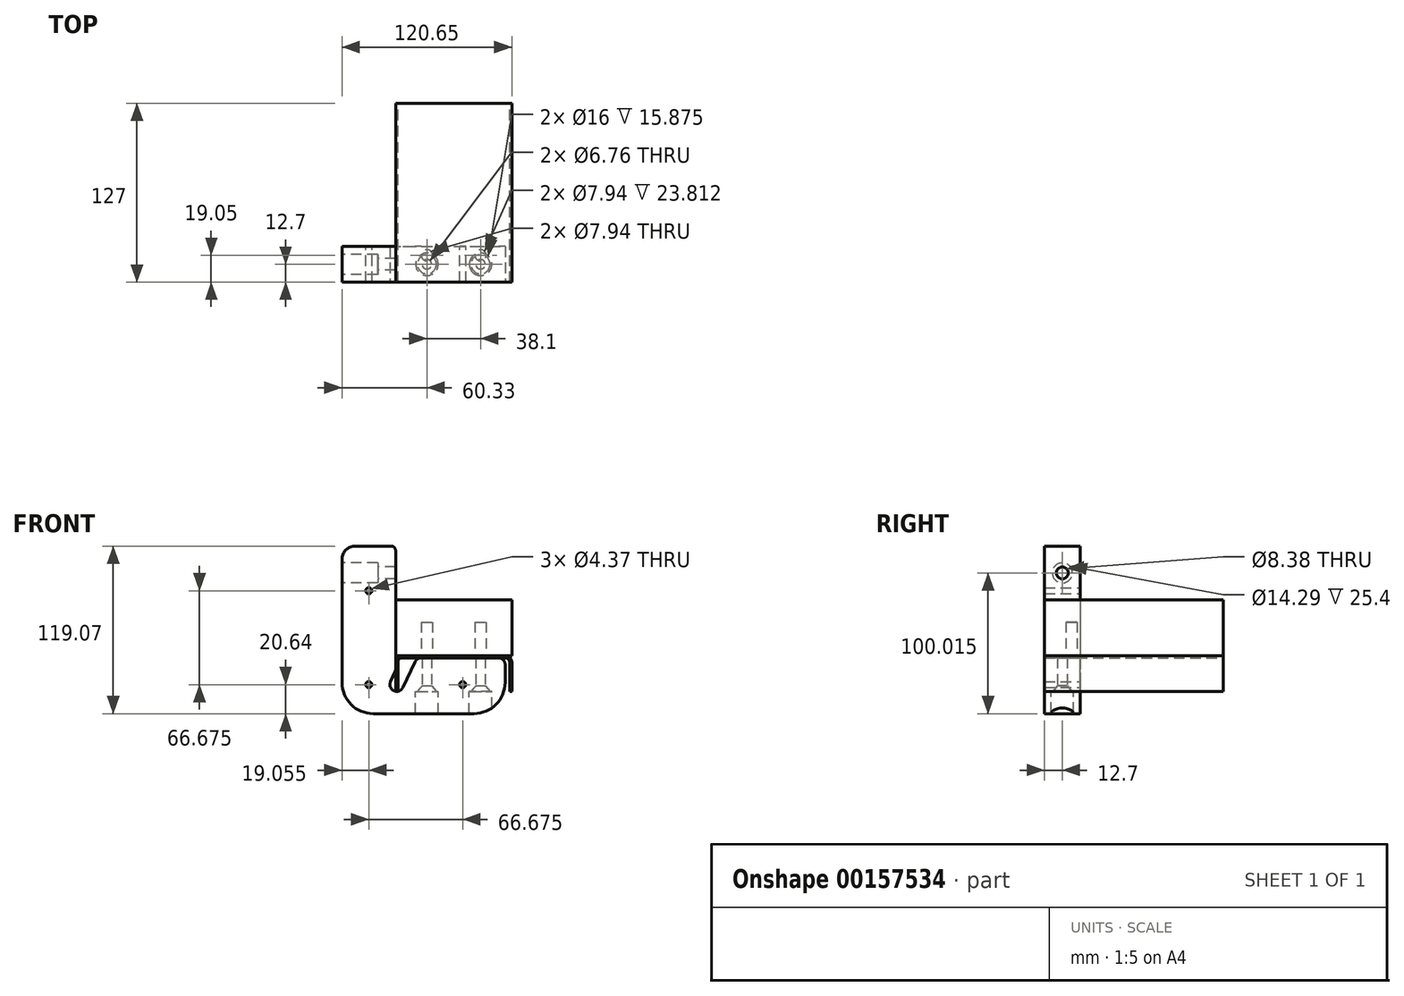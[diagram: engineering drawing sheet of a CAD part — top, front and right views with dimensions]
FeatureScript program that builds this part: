
annotation { "Feature Type Name" : "Feature", "Feature Type Description" : "" }
export const myFeature = defineFeature(function(context is Context, id is Id, definition is map)
    precondition{}
    {
        {
            var Q0;
            Q0=qCreatedBy(makeId("Front.planeOp"),FACE);
            var sketch = newSketch(context, id + "F0", { "sketchPlane" : qUnion([Q0])});
            skLineSegment(sketch, "E0", {"start": v(41.28, -23.81) * mm, "end": v(41.28, -3.17) * mm});
            skLineSegment(sketch, "E1", {"start": v(36.51, 1.59) * mm, "end": v(-36.51, 1.59) * mm});
            skLineSegment(sketch, "E2", {"start": v(-41.27, -3.18) * mm, "end": v(-41.27, -23.81) * mm});
            skLineSegment(sketch, "E3", {"start": v(-41.28, -23.81) * mm, "end": v(-39.69, -23.81) * mm});
            skLineSegment(sketch, "E4", {"start": v(-39.69, -23.81) * mm, "end": v(-39.69, -3.18) * mm});
            skLineSegment(sketch, "E5", {"start": v(-36.51, 0) * mm, "end": v(36.51, 0) * mm});
            skLineSegment(sketch, "E6", {"start": v(39.69, -3.17) * mm, "end": v(39.69, -23.81) * mm});
            skLineSegment(sketch, "E7", {"start": v(39.69, -23.81) * mm, "end": v(41.28, -23.81) * mm});
            skLineSegment(sketch, "E8", {"start": v(0, 0) * mm, "end": v(0, 1.59) * mm, "construction": true});
            skPoint(sketch, "E9.visualSharp", {"position": v(-39.69, 0) * mm});
            skArc(sketch, "E9.filletArc", {"start": v(-36.51, 0) * mm, "mid": v(-38.76, -0.93) * mm, "end": v(-39.69, -3.18) * mm});
            skPoint(sketch, "E10.visualSharp", {"position": v(39.69, 0) * mm});
            skArc(sketch, "E10.filletArc", {"start": v(39.69, -3.17) * mm, "mid": v(38.76, -0.93) * mm, "end": v(36.51, 0) * mm});
            skPoint(sketch, "E11.visualSharp", {"position": v(-41.28, 1.59) * mm});
            skArc(sketch, "E11.filletArc", {"start": v(-36.51, 1.59) * mm, "mid": v(-39.88, 0.2) * mm, "end": v(-41.28, -3.18) * mm});
            skPoint(sketch, "E12.visualSharp", {"position": v(41.28, 1.59) * mm});
            skArc(sketch, "E12.filletArc", {"start": v(41.28, -3.17) * mm, "mid": v(39.88, 0.2) * mm, "end": v(36.51, 1.59) * mm});
            skSolve(sketch);
        }
        {
            var Q0;
            Q0 = qSketchRegion(id + "F0", true);
            extrude(context, id + "F1", {"entities" : qUnion([Q0]), "depth" : 127 * mm});
        }
        {
            var Q0;
            Q0=makeQuery(id+"F1.opExtrude","CAP_FACE",FACE,{"disambiguationData":[OSD([sQuery(id+"F0.wireOp",EDGE,"E0"),sQuery(id+"F0.wireOp",EDGE,"E1"),sQuery(id+"F0.wireOp",EDGE,"E2"),sQuery(id+"F0.wireOp",EDGE,"E3"),sQuery(id+"F0.wireOp",EDGE,"E4"),sQuery(id+"F0.wireOp",EDGE,"E5"),sQuery(id+"F0.wireOp",EDGE,"E6"),sQuery(id+"F0.wireOp",EDGE,"E7"),sQuery(id+"F0.wireOp",EDGE,"E9.filletArc"),sQuery(id+"F0.wireOp",EDGE,"E10.filletArc"),sQuery(id+"F0.wireOp",EDGE,"E11.filletArc"),sQuery(id+"F0.wireOp",EDGE,"E12.filletArc")])],"isStart":false});
            var sketch = newSketch(context, id + "F2", { "sketchPlane" : qUnion([Q0])});
            skLineSegment(sketch, "E13.bottom", {"start": v(-41.28, 1.59) * mm, "end": v(41.28, 1.59) * mm});
            skLineSegment(sketch, "E13.top", {"start": v(-41.28, 41.27) * mm, "end": v(41.27, 41.27) * mm});
            skLineSegment(sketch, "E13.left", {"start": v(-41.28, 1.59) * mm, "end": v(-41.28, 41.27) * mm});
            skLineSegment(sketch, "E13.right", {"start": v(41.28, 1.59) * mm, "end": v(41.27, 41.27) * mm});
            skSolve(sketch);
        }
        {
            var Q0;
            Q0 = qSketchRegion(id + "F2", true);
            var Q1;
            Q1=makeQuery(id+"F1.opExtrude","CAP_FACE",FACE,{"disambiguationData":[OSD([sQuery(id+"F0.wireOp",EDGE,"E0"),sQuery(id+"F0.wireOp",EDGE,"E1"),sQuery(id+"F0.wireOp",EDGE,"E2"),sQuery(id+"F0.wireOp",EDGE,"E3"),sQuery(id+"F0.wireOp",EDGE,"E4"),sQuery(id+"F0.wireOp",EDGE,"E5"),sQuery(id+"F0.wireOp",EDGE,"E6"),sQuery(id+"F0.wireOp",EDGE,"E7"),sQuery(id+"F0.wireOp",EDGE,"E9.filletArc"),sQuery(id+"F0.wireOp",EDGE,"E10.filletArc"),sQuery(id+"F0.wireOp",EDGE,"E11.filletArc"),sQuery(id+"F0.wireOp",EDGE,"E12.filletArc")])],"isStart":true});
            extrude(context, id + "F3", {"entities" : qUnion([Q0]), "endBound" : BoundingType.UP_TO_SURFACE, "oppositeDirection" : true, "endBoundEntityFace" : qUnion([Q1]), "depth" : 25.4 * mm});
        }
        {
            var Q0;
            Q0=makeQuery(id+"F1.opExtrude","SWEPT_FACE",FACE,{"disambiguationData":[OSD([sQuery(id+"F0.wireOp",EDGE,"E5")])]});
            var sketch = newSketch(context, id + "F4", { "sketchPlane" : qUnion([Q0])});
            skCircle(sketch, "E14", {"center": v(-19.05, 107.95) * mm, "radius": 3.97 * mm});
            skCircle(sketch, "E15", {"center": v(19.05, 107.95) * mm, "radius": 3.97 * mm});
            skLineSegment(sketch, "E16", {"start": v(-19.05, 107.95) * mm, "end": v(-36.51, 107.95) * mm, "construction": true});
            skLineSegment(sketch, "E17", {"start": v(19.05, 107.95) * mm, "end": v(36.51, 107.95) * mm, "construction": true});
            skSolve(sketch);
        }
        {
            var Q0;
            Q0 = qSketchRegion(id + "F4", true);
            extrude(context, id + "F5", {"entities" : qUnion([Q0]), "operationType" : NewBodyOperationType.REMOVE, "oppositeDirection" : true, "depth" : 25.4 * mm});
        }
        {
            var Q0;
            Q0=makeQuery(id+"F1.opExtrude","CAP_FACE",FACE,{"disambiguationData":[OSD([sQuery(id+"F0.wireOp",EDGE,"E0"),sQuery(id+"F0.wireOp",EDGE,"E1"),sQuery(id+"F0.wireOp",EDGE,"E2"),sQuery(id+"F0.wireOp",EDGE,"E3"),sQuery(id+"F0.wireOp",EDGE,"E4"),sQuery(id+"F0.wireOp",EDGE,"E5"),sQuery(id+"F0.wireOp",EDGE,"E6"),sQuery(id+"F0.wireOp",EDGE,"E7"),sQuery(id+"F0.wireOp",EDGE,"E9.filletArc"),sQuery(id+"F0.wireOp",EDGE,"E10.filletArc"),sQuery(id+"F0.wireOp",EDGE,"E11.filletArc"),sQuery(id+"F0.wireOp",EDGE,"E12.filletArc")])],"isStart":false});
            var sketch = newSketch(context, id + "F6", { "sketchPlane" : qUnion([Q0])});
            skLineSegment(sketch, "E18", {"start": v(-41.28, 79.38) * mm, "end": v(-79.38, 79.38) * mm});
            skLineSegment(sketch, "E19", {"start": v(-79.38, 79.38) * mm, "end": v(-79.38, -39.69) * mm});
            skLineSegment(sketch, "E20", {"start": v(-79.37, -39.69) * mm, "end": v(36.51, -39.69) * mm});
            skLineSegment(sketch, "E21", {"start": v(36.51, -39.69) * mm, "end": v(36.51, -4.76) * mm});
            skLineSegment(sketch, "E22", {"start": v(31.75, 0) * mm, "end": v(-26.2, 0) * mm});
            skPoint(sketch, "E23.visualSharp", {"position": v(36.51, 0) * mm});
            skArc(sketch, "E23.filletArc", {"start": v(36.51, -4.76) * mm, "mid": v(35.12, -1.4) * mm, "end": v(31.75, 0) * mm});
            skCircle(sketch, "E24", {"center": v(-19.05, -8.8) * mm, "radius": 3.97 * mm, "construction": true});
            skCircle(sketch, "E25", {"center": v(19.05, -8.8) * mm, "radius": 3.97 * mm, "construction": true});
            skLineSegment(sketch, "E26", {"start": v(-19.05, -8.8) * mm, "end": v(19.05, -8.8) * mm, "construction": true});
            skLineSegment(sketch, "E27", {"start": v(0, -8.8) * mm, "end": v(0, 0) * mm, "construction": true});
            skLineSegment(sketch, "E28", {"start": v(-19.05, -8.8) * mm, "end": v(-23.02, -8.8) * mm, "construction": true});
            skLineSegment(sketch, "E29", {"start": v(-41.28, -9.1) * mm, "end": v(-41.28, 79.38) * mm});
            skLineSegment(sketch, "E30", {"start": v(-36.11, -21.1) * mm, "end": v(-26.2, 0) * mm});
            skLineSegment(sketch, "E31", {"start": v(-44.88, -17.06) * mm, "end": v(-41.28, -9.1) * mm});
            skArc(sketch, "E32", {"start": v(-44.88, -17.06) * mm, "mid": v(-42.5, -23.43) * mm, "end": v(-36.11, -21.1) * mm});
            skPoint(sketch, "E33", {"position": v(-41.27, -13.5) * mm});
            skCircle(sketch, "E34", {"center": v(-36.82, -11.11) * mm, "radius": 4.89 * mm, "construction": true});
            skSolve(sketch);
        }
        {
            var Q0;
            {var subQ6=sQuery(id+"F6.wireOp",EDGE,"E18");Q0=makeQuery(id+"F6.imprint","IMPRINT",FACE,{"disambiguationData":[TD([[makeQuery(id+"F6.imprint","IMPRINT",EDGE,{"derivedFrom":subQ6}),1.0]])]});}
            extrude(context, id + "F7", {"entities" : qUnion([Q0]), "oppositeDirection" : true, "depth" : 25.4 * mm});
        }
        {
            var Q0;
            Q0=makeQuery(id+"F7.opExtrude","SWEPT_EDGE",EDGE,{"disambiguationData":[OSD([sQuery(id+"F6.wireOp",EDGE,"E19"),sQuery(id+"F6.wireOp",EDGE,"E20")])]});
            var Q1;
            Q1=makeQuery(id+"F7.opExtrude","SWEPT_EDGE",EDGE,{"disambiguationData":[OSD([sQuery(id+"F6.wireOp",EDGE,"E20"),sQuery(id+"F6.wireOp",EDGE,"E21")])]});
            fillet(context, id + "F8", {"entities" : qUnion([Q0, Q1]), "radius" : 22.22 * mm, "tangentPropagation" : true, "allowEdgeOverflow" : false});
        }
        {
            var Q0;
            Q0=makeQuery(id+"F7.opExtrude","SWEPT_FACE",FACE,{"disambiguationData":[OSD([sQuery(id+"F6.wireOp",EDGE,"E20")])]});
            cPlane(context, id + "F9", {"entities" : qUnion([Q0]), "cplaneType" : CPlaneType.OFFSET, "offset" : 15.88 * mm, "oppositeDirection" : true, "width" : 152.4 * mm, "height" : 152.4 * mm});
        }
        {
            var Q0;
            Q0=qCreatedBy(id+"F9.planeOp",FACE);
            var sketch = newSketch(context, id + "F10", { "sketchPlane" : qUnion([Q0])});
            skPoint(sketch, "E35", {"position": v(-19.05, 114.3) * mm});
            skPoint(sketch, "E36", {"position": v(19.05, 114.3) * mm});
            skLineSegment(sketch, "E37", {"start": v(19.05, 114.3) * mm, "end": v(19.05, 107.95) * mm, "construction": true});
            skLineSegment(sketch, "E38", {"start": v(-19.05, 114.3) * mm, "end": v(-19.05, 107.95) * mm, "construction": true});
            skLineSegment(sketch, "E39", {"start": v(-19.05, 114.3) * mm, "end": v(-57.15, 114.3) * mm, "construction": true});
            skPoint(sketch, "E40", {"position": v(-60.33, 114.3) * mm});
            skCircle(sketch, "E41", {"center": v(-19.05, 114.3) * mm, "radius": 8 * mm});
            skCircle(sketch, "E42", {"center": v(19.05, 114.3) * mm, "radius": 8 * mm});
            skSolve(sketch);
        }
        {
            var Q0;
            Q0 = qSketchRegion(id + "F10", true);
            extrude(context, id + "F11", {"entities" : qUnion([Q0]), "operationType" : NewBodyOperationType.REMOVE, "depth" : 25.4 * mm});
        }
        {
            var Q0;
            Q0=sQuery(id+"F10.wireOp",VERTEX,"E35");
            var Q1;
            Q1=sQuery(id+"F10.wireOp",VERTEX,"E36");
            var Q2;
            Q2=makeQuery(id+"F7.opExtrude","SWEPT_BODY",BODY,{"disambiguationData":[OSD([sQuery(id+"F6.wireOp",EDGE,"E18"),sQuery(id+"F6.wireOp",EDGE,"E19"),sQuery(id+"F6.wireOp",EDGE,"E20"),sQuery(id+"F6.wireOp",EDGE,"E21"),sQuery(id+"F6.wireOp",EDGE,"E22"),sQuery(id+"F6.wireOp",EDGE,"VCN7EzUT-UCgr-9Dl2-yQ6i-yJvqr16Mm8If"),sQuery(id+"F6.wireOp",EDGE,"28iwqmir-5wwE-XKHo-pBXU-8pbr5TsYityO"),sQuery(id+"F6.wireOp",EDGE,"E23.filletArc"),sQuery(id+"F6.wireOp",EDGE,"5D1ydIdo-Vbug-DlCE-rGqy-j11egtTWor9N"),sQuery(id+"F6.wireOp",EDGE,"fc85a2f7-f7e6-4432-93fa-4e404d59246a.filletArc")])]});
            hole(context, id + "F12", {"style" : HoleStyle.C_SINK, "endStyle" : HoleEndStyle.THROUGH, "standardTappedOrClearance" : lookupTablePath({ "fit" : "Free", "standard" : "ANSI", "size" : "1/4", "type" : "Clearance" }), "standardBlindInLast" : lookupTablePath({ "fit" : "Free", "standard" : "ANSI", "engagement" : "75%", "pitch" : "20 tpi", "size" : "1/4", "type" : "Clearance & tapped" }), "holeDiameter" : 6.76 * mm, "cSinkDiameter" : 13.5 * mm, "cSinkAngle" : 82 * degree, "majorDiameter" : 6.35 * mm, "locations" : qUnion([Q0, Q1]), "scope" : qUnion([Q2]), "isTappedThrough" : true, "tappedDepth" : 12.7 * mm, "tapClearance" : 3});
        }
        {
            var Q0;
            Q0=makeQuery(id+"F7.opExtrude","SWEPT_EDGE",EDGE,{"disambiguationData":[OSD([sQuery(id+"F6.wireOp",EDGE,"E18"),sQuery(id+"F6.wireOp",EDGE,"E29")])]});
            fillet(context, id + "F13", {"entities" : qUnion([Q0]), "radius" : 3.17 * mm, "tangentPropagation" : true, "allowEdgeOverflow" : false});
        }
        {
            var Q0;
            Q0=makeQuery(id+"F7.opExtrude","SWEPT_EDGE",EDGE,{"disambiguationData":[OSD([sQuery(id+"F6.wireOp",EDGE,"E18"),sQuery(id+"F6.wireOp",EDGE,"E19")])]});
            fillet(context, id + "F14", {"entities" : qUnion([Q0]), "radius" : 9.52 * mm, "tangentPropagation" : true, "allowEdgeOverflow" : false});
        }
        {
            var Q0;
            Q0=makeQuery(id+"F7.opExtrude","SWEPT_FACE",FACE,{"disambiguationData":[OSD([sQuery(id+"F6.wireOp",EDGE,"E19")])]});
            var sketch = newSketch(context, id + "F15", { "sketchPlane" : qUnion([Q0])});
            skPoint(sketch, "E43", {"position": v(114.3, 60.33) * mm});
            skLineSegment(sketch, "E44", {"start": v(101.6, 60.33) * mm, "end": v(127, 60.33) * mm, "construction": true});
            skSolve(sketch);
        }
        {
            var Q0;
            Q0=sQuery(id+"F15.wireOp",VERTEX,"E43");
            var Q1;
            Q1=makeQuery(id+"F7.opExtrude","SWEPT_BODY",BODY,{"disambiguationData":[OSD([sQuery(id+"F6.wireOp",EDGE,"E18"),sQuery(id+"F6.wireOp",EDGE,"E19"),sQuery(id+"F6.wireOp",EDGE,"E20"),sQuery(id+"F6.wireOp",EDGE,"E21"),sQuery(id+"F6.wireOp",EDGE,"E22"),sQuery(id+"F6.wireOp",EDGE,"E23.filletArc"),sQuery(id+"F6.wireOp",EDGE,"E29"),sQuery(id+"F6.wireOp",EDGE,"E30"),sQuery(id+"F6.wireOp",EDGE,"E31"),sQuery(id+"F6.wireOp",EDGE,"E32")])]});
            hole(context, id + "F16", {"style" : HoleStyle.C_BORE, "endStyle" : HoleEndStyle.THROUGH, "holeDiameter" : 8.38 * mm, "cBoreDiameter" : 14.29 * mm, "cBoreDepth" : 25.4 * mm, "locations" : qUnion([Q0]), "scope" : qUnion([Q1]), "isTappedThrough" : true});
        }
        {
            var Q0;
            Q0=makeQuery(id+"F7.opExtrude","SWEPT_EDGE",EDGE,{"disambiguationData":[OSD([sQuery(id+"F0.wireOp",EDGE,"E2"),sQuery(id+"F6.wireOp",EDGE,"E29"),sQuery(id+"F6.wireOp",EDGE,"E31")])]});
            var Q1;
            Q1=makeQuery(id+"F7.opExtrude","SWEPT_EDGE",EDGE,{"disambiguationData":[OSD([sQuery(id+"F0.wireOp",EDGE,"E5"),sQuery(id+"F6.wireOp",EDGE,"E22"),sQuery(id+"F6.wireOp",EDGE,"E30")])]});
            fillet(context, id + "F17", {"entities" : qUnion([Q0, Q1]), "radius" : 5.08 * mm, "tangentPropagation" : true, "allowEdgeOverflow" : false});
        }
        {
            var Q0;
            Q0=makeQuery(id+"F7.opExtrude","CAP_FACE",FACE,{"disambiguationData":[OSD([sQuery(id+"F6.wireOp",EDGE,"E18"),sQuery(id+"F6.wireOp",EDGE,"E19"),sQuery(id+"F6.wireOp",EDGE,"E20"),sQuery(id+"F6.wireOp",EDGE,"E21"),sQuery(id+"F6.wireOp",EDGE,"E22"),sQuery(id+"F6.wireOp",EDGE,"E23.filletArc"),sQuery(id+"F6.wireOp",EDGE,"E29"),sQuery(id+"F6.wireOp",EDGE,"E30"),sQuery(id+"F6.wireOp",EDGE,"E31"),sQuery(id+"F6.wireOp",EDGE,"E32")])],"isStart":false});
            var sketch = newSketch(context, id + "F18", { "sketchPlane" : qUnion([Q0])});
            skCircle(sketch, "E45", {"center": v(60.33, 47.62) * mm, "radius": 2.18 * mm});
            skCircle(sketch, "E46", {"center": v(60.33, -19.05) * mm, "radius": 2.18 * mm});
            skCircle(sketch, "E47", {"center": v(-6.35, -19.05) * mm, "radius": 2.18 * mm});
            skLineSegment(sketch, "E48", {"start": v(41.28, 20.33) * mm, "end": v(79.38, 20.33) * mm, "construction": true});
            skLineSegment(sketch, "E49", {"start": v(60.33, 20.33) * mm, "end": v(60.33, -19.05) * mm, "construction": true});
            skSolve(sketch);
        }
        {
            var Q0;
            Q0 = qSketchRegion(id + "F18", true);
            extrude(context, id + "F19", {"entities" : qUnion([Q0]), "operationType" : NewBodyOperationType.REMOVE, "endBound" : BoundingType.THROUGH_ALL, "oppositeDirection" : true, "depth" : 25.4 * mm});
        }
    });
